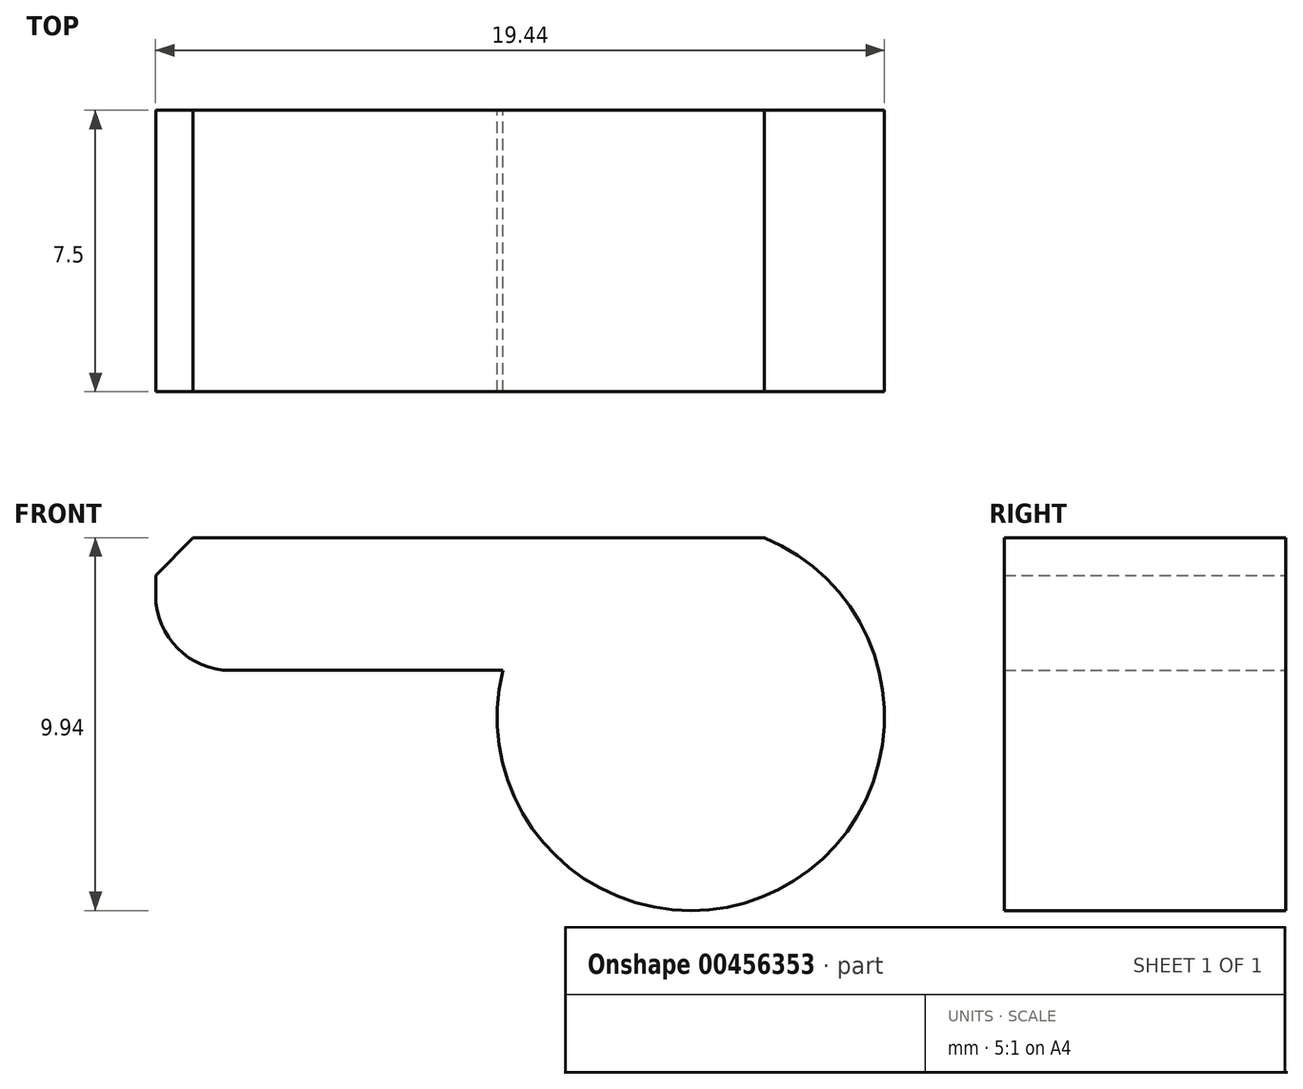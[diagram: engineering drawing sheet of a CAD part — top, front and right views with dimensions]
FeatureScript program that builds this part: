
annotation { "Feature Type Name" : "Feature", "Feature Type Description" : "" }
export const myFeature = defineFeature(function(context is Context, id is Id, definition is map)
    precondition{}
    {
        {
            var Q0;
            Q0=qCreatedBy(makeId("Front.planeOp"),FACE);
            var sketch = newSketch(context, id + "F0", { "sketchPlane" : qUnion([Q0])});
            skLineSegment(sketch, "E0", {"start": v(-8.59, 8.58) * mm, "end": v(7.65, 8.58) * mm});
            skLineSegment(sketch, "E1", {"start": v(-8.59, 8.58) * mm, "end": v(-8.59, 5.04) * mm});
            skLineSegment(sketch, "E2", {"start": v(-8.59, 5.04) * mm, "end": v(0.67, 5.04) * mm});
            skArc(sketch, "E3", {"start": v(0.67, 5.04) * mm, "mid": v(8.02, -0.8) * mm, "end": v(7.65, 8.58) * mm});
            skSolve(sketch);
        }
        {
            var Q0;
            Q0=makeQuery(id+"F0.imprint","IMPRINT",FACE,{"disambiguationData":[TD([[makeQuery(id+"F0.imprint","IMPRINT",EDGE,{"derivedFrom":sQuery(id+"F0.wireOp",EDGE,"E0")}),-1.0]])]});
            extrude(context, id + "F1", {"entities" : qUnion([Q0]), "depth" : 7.5 * mm});
        }
        {
            var Q0;
            Q0=makeQuery(id+"F1.opExtrude","SWEPT_EDGE",EDGE,{"disambiguationData":[OSD([sQuery(id+"F0.wireOp",EDGE,"E1"),sQuery(id+"F0.wireOp",EDGE,"E2")])]});
            fillet(context, id + "F2", {"entities" : qUnion([Q0]), "radius" : 2 * mm, "tangentPropagation" : true, "allowEdgeOverflow" : false});
        }
        {
            var Q0;
            Q0=makeQuery(id+"F1.opExtrude","SWEPT_EDGE",EDGE,{"disambiguationData":[OSD([sQuery(id+"F0.wireOp",EDGE,"E0"),sQuery(id+"F0.wireOp",EDGE,"E1")])]});
            chamfer(context, id + "F3", {"entities" : qUnion([Q0]), "width" : 1 * mm, "tangentPropagation" : true});
        }
    });
